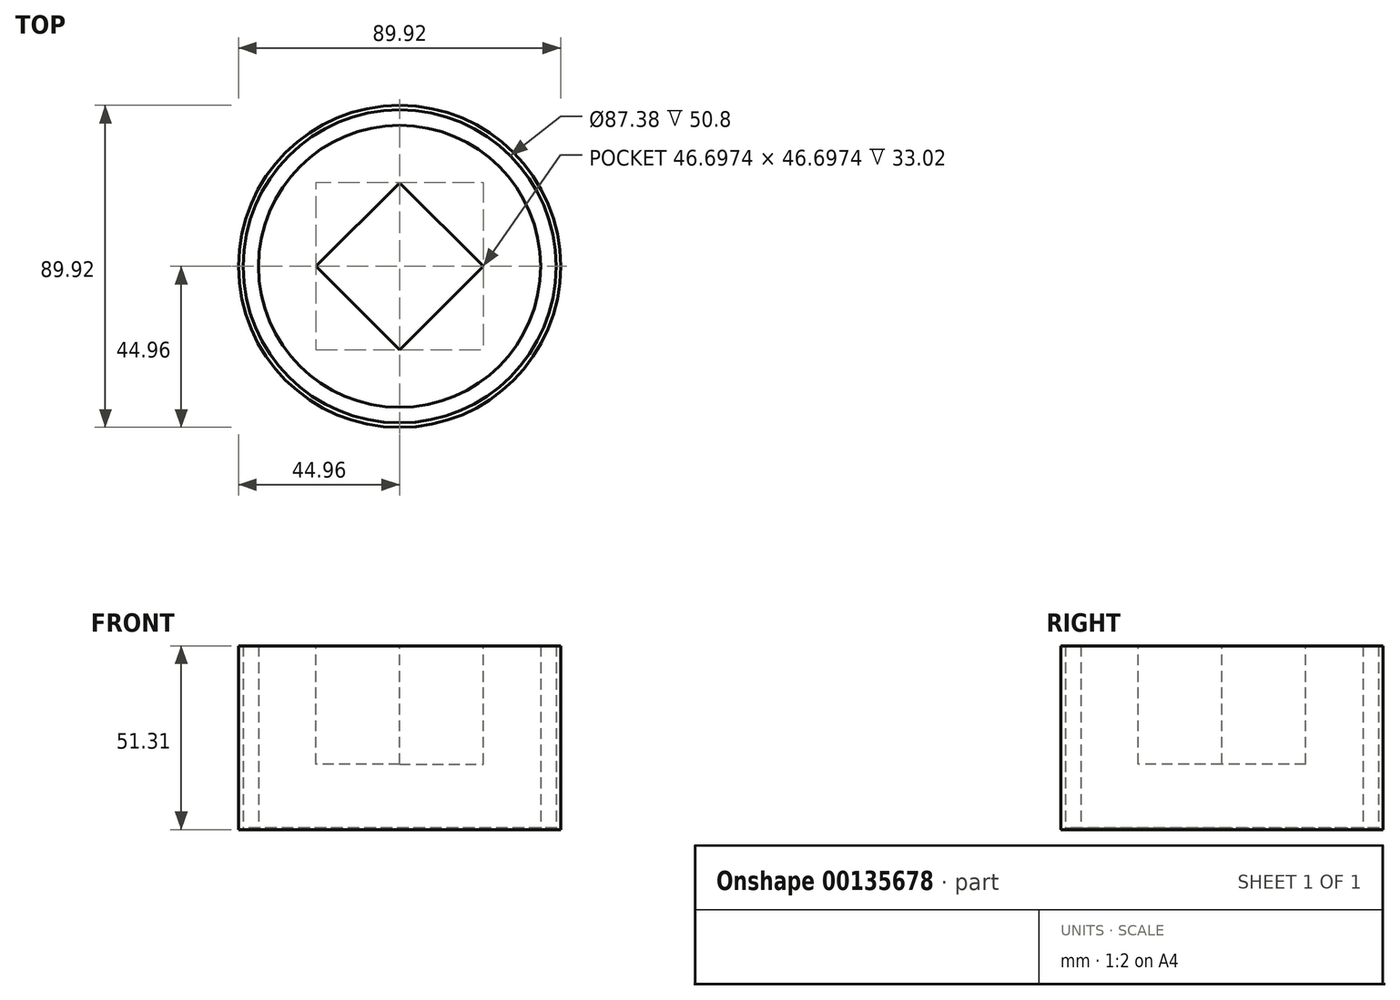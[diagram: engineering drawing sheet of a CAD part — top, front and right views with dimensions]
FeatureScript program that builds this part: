
annotation { "Feature Type Name" : "Feature", "Feature Type Description" : "" }
export const myFeature = defineFeature(function(context is Context, id is Id, definition is map)
    precondition{}
    {
        {
            var Q0;
            Q0=qCreatedBy(makeId("Top.planeOp"),FACE);
            var sketch = newSketch(context, id + "F0", { "sketchPlane" : qUnion([Q0])});
            skCircle(sketch, "E0", {"center": v(0, 0) * mm, "radius": 44.96 * mm});
            skSolve(sketch);
        }
        {
            var Q0;
            Q0=sQuery(id+"F0.wireOp",EDGE,"E0");
            extrude(context, id + "F1", {"bodyType" : ToolBodyType.SURFACE, "surfaceEntities" : qUnion([Q0]), "depth" : 50.8 * mm});
        }
        {
            var Q0;
            Q0=qCreatedBy(makeId("Top.planeOp"),FACE);
            var sketch = newSketch(context, id + "F2", { "sketchPlane" : qUnion([Q0])});
            skCircle(sketch, "E1", {"center": v(0, 0) * mm, "radius": 44.96 * mm});
            skSolve(sketch);
        }
        {
            var Q0;
            Q0 = qSketchRegion(id + "F2", true);
            extrude(context, id + "F3", {"entities" : qUnion([Q0]), "oppositeDirection" : true, "depth" : 0.5 * mm});
        }
        {
            var Q0;
            Q0=qCreatedBy(makeId("Top.planeOp"),FACE);
            var sketch = newSketch(context, id + "F4", { "sketchPlane" : qUnion([Q0])});
            skCircle(sketch, "E2", {"center": v(0, 0) * mm, "radius": 39.37 * mm});
            skSolve(sketch);
        }
        {
            var Q0;
            Q0 = qSketchRegion(id + "F4", true);
            extrude(context, id + "F5", {"entities" : qUnion([Q0]), "operationType" : NewBodyOperationType.ADD, "depth" : 50.8 * mm});
        }
        {
            var Q0;
            Q0=makeQuery(id+"F5.opExtrude","CAP_FACE",FACE,{"disambiguationData":[OSD([sQuery(id+"F4.wireOp",EDGE,"E2")])],"isStart":false});
            var sketch = newSketch(context, id + "F6", { "sketchPlane" : qUnion([Q0])});
            skLineSegment(sketch, "E3.bottom", {"start": v(0, 23.35) * mm, "end": v(-23.35, 0) * mm});
            skLineSegment(sketch, "E3.top", {"start": v(23.35, 0) * mm, "end": v(0, -23.35) * mm});
            skLineSegment(sketch, "E3.left", {"start": v(0, 23.35) * mm, "end": v(23.35, 0) * mm});
            skLineSegment(sketch, "E3.right", {"start": v(-23.35, 0) * mm, "end": v(0, -23.35) * mm});
            skPoint(sketch, "E3.middle", {"position": v(0, 0) * mm});
            skSolve(sketch);
        }
        {
            var Q0;
            Q0 = qSketchRegion(id + "F6", true);
            extrude(context, id + "F7", {"entities" : qUnion([Q0]), "operationType" : NewBodyOperationType.REMOVE, "oppositeDirection" : true, "depth" : 33.02 * mm});
        }
        {
            var Q0;
            Q0=qCreatedBy(makeId("Top.planeOp"),FACE);
            var sketch = newSketch(context, id + "F8", { "sketchPlane" : qUnion([Q0])});
            skCircle(sketch, "E4", {"center": v(0, 0) * mm, "radius": 44.96 * mm});
            skCircle(sketch, "E5", {"center": v(0, 0) * mm, "radius": 43.69 * mm});
            skSolve(sketch);
        }
        {
            var Q0;
            Q0 = qSketchRegion(id + "F8", true);
            extrude(context, id + "F9", {"entities" : qUnion([Q0]), "operationType" : NewBodyOperationType.ADD, "depth" : 50.8 * mm});
        }
    });
